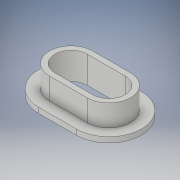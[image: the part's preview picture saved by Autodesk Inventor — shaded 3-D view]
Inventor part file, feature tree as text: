
AUTODESK INVENTOR PART (.ipt)
format: ipt  version: 2017 (Build 210142000, 142)  size: 133,120 bytes
history: native  units: mm
features: extrude x3, sketch x3, projected_geometry x2, other x1
ambient origin geometry x8: Origin, YZ Plane, XZ Plane, XY Plane, X Axis, Y Axis, Z Axis, Center Point
bodies: Body1 (feature_tree)
feature tree (9):
  other  "Твердое тело1"
  extrude  "Выдавливание1"  Depth=7.0mm
  extrude  "Выдавливание2"  Depth=8.0mm
  extrude  "Выдавливание3"  Depth=5.0mm TaperAngle=0.0deg
  sketch  "Эскиз1"
  sketch  "Эскиз2"
  projected_geometry  "Спроецированная петля1"
  sketch  "Эскиз3"
  projected_geometry  "Спроецированная петля2"
